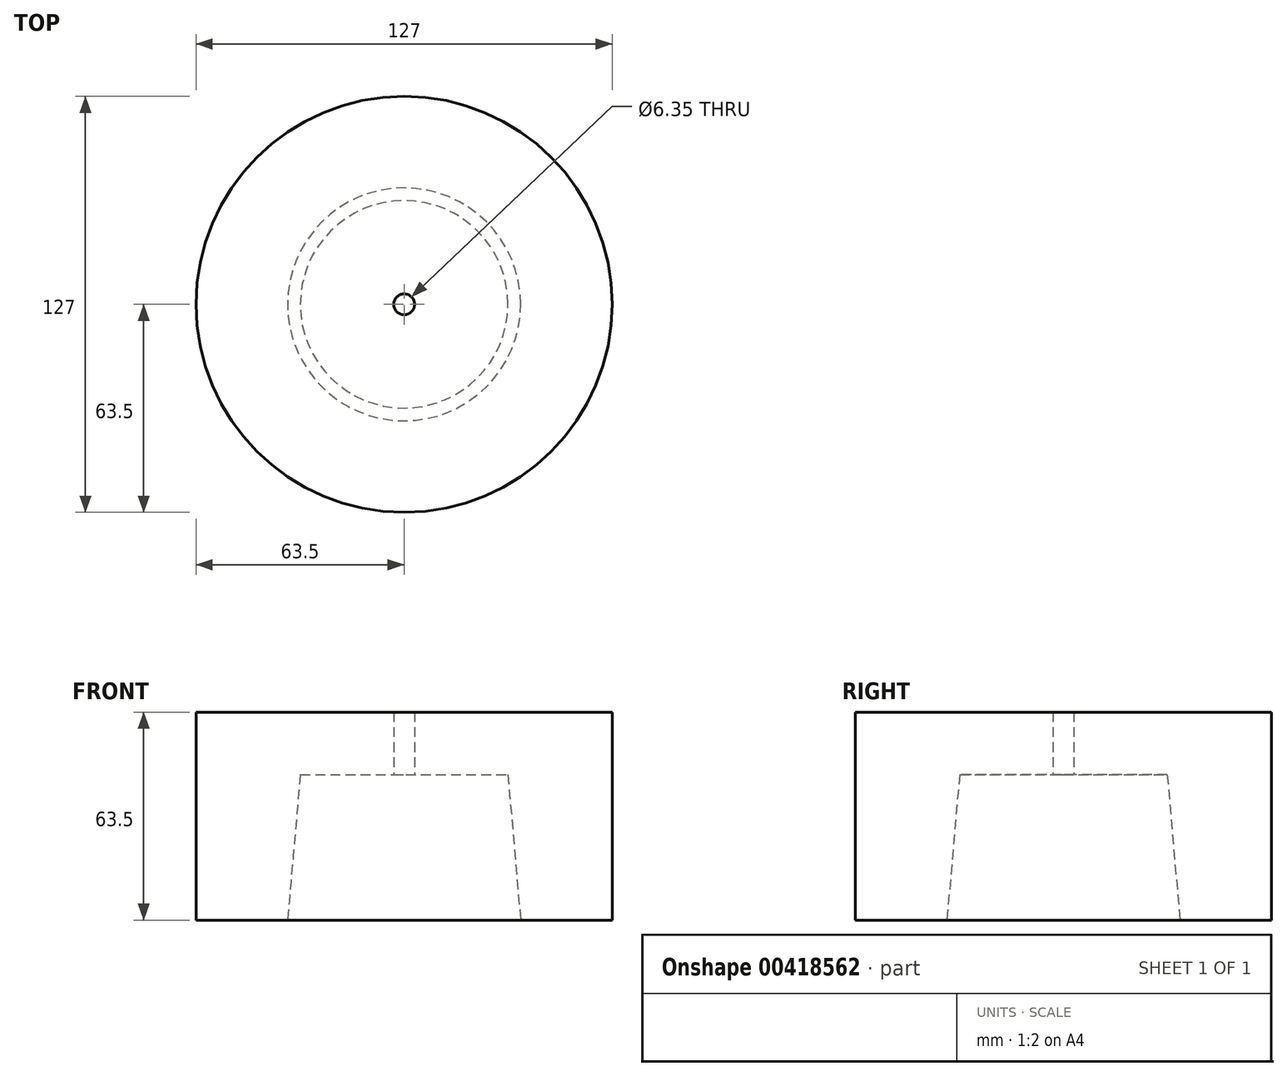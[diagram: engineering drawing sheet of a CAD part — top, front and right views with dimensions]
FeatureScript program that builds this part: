
annotation { "Feature Type Name" : "Feature", "Feature Type Description" : "" }
export const myFeature = defineFeature(function(context is Context, id is Id, definition is map)
    precondition{}
    {
        {
            var Q0;
            Q0=qCreatedBy(makeId("Front.planeOp"),FACE);
            var sketch = newSketch(context, id + "F0", { "sketchPlane" : qUnion([Q0])});
            skLineSegment(sketch, "E0", {"start": v(-3.18, 63.5) * mm, "end": v(-63.5, 63.5) * mm});
            skLineSegment(sketch, "E1", {"start": v(-63.5, 63.5) * mm, "end": v(-63.5, 0) * mm});
            skLineSegment(sketch, "E2", {"start": v(-63.5, 0) * mm, "end": v(-35.56, 0) * mm});
            skLineSegment(sketch, "E3", {"start": v(-35.56, 0) * mm, "end": v(-31.67, 44.45) * mm});
            skLineSegment(sketch, "E4", {"start": v(-31.67, 44.45) * mm, "end": v(-3.18, 44.45) * mm});
            skLineSegment(sketch, "E5", {"start": v(-3.18, 44.45) * mm, "end": v(-3.18, 63.5) * mm});
            skLineSegment(sketch, "E6", {"start": v(0, 0) * mm, "end": v(0, 60.83) * mm});
            skSolve(sketch);
        }
        {
            var Q0;
            Q0=makeQuery(id+"F0.imprint","IMPRINT",FACE,{"disambiguationData":[TD([[makeQuery(id+"F0.imprint","IMPRINT",EDGE,{"derivedFrom":sQuery(id+"F0.wireOp",EDGE,"E0")}),1.0]])]});
            var Q1;
            Q1=sQuery(id+"F0.wireOp",EDGE,"E6");
            revolve(context, id + "F1", {"entities" : qUnion([Q0]), "axis" : qUnion([Q1]), "revolveType" : RevolveType.FULL});
        }
    });
